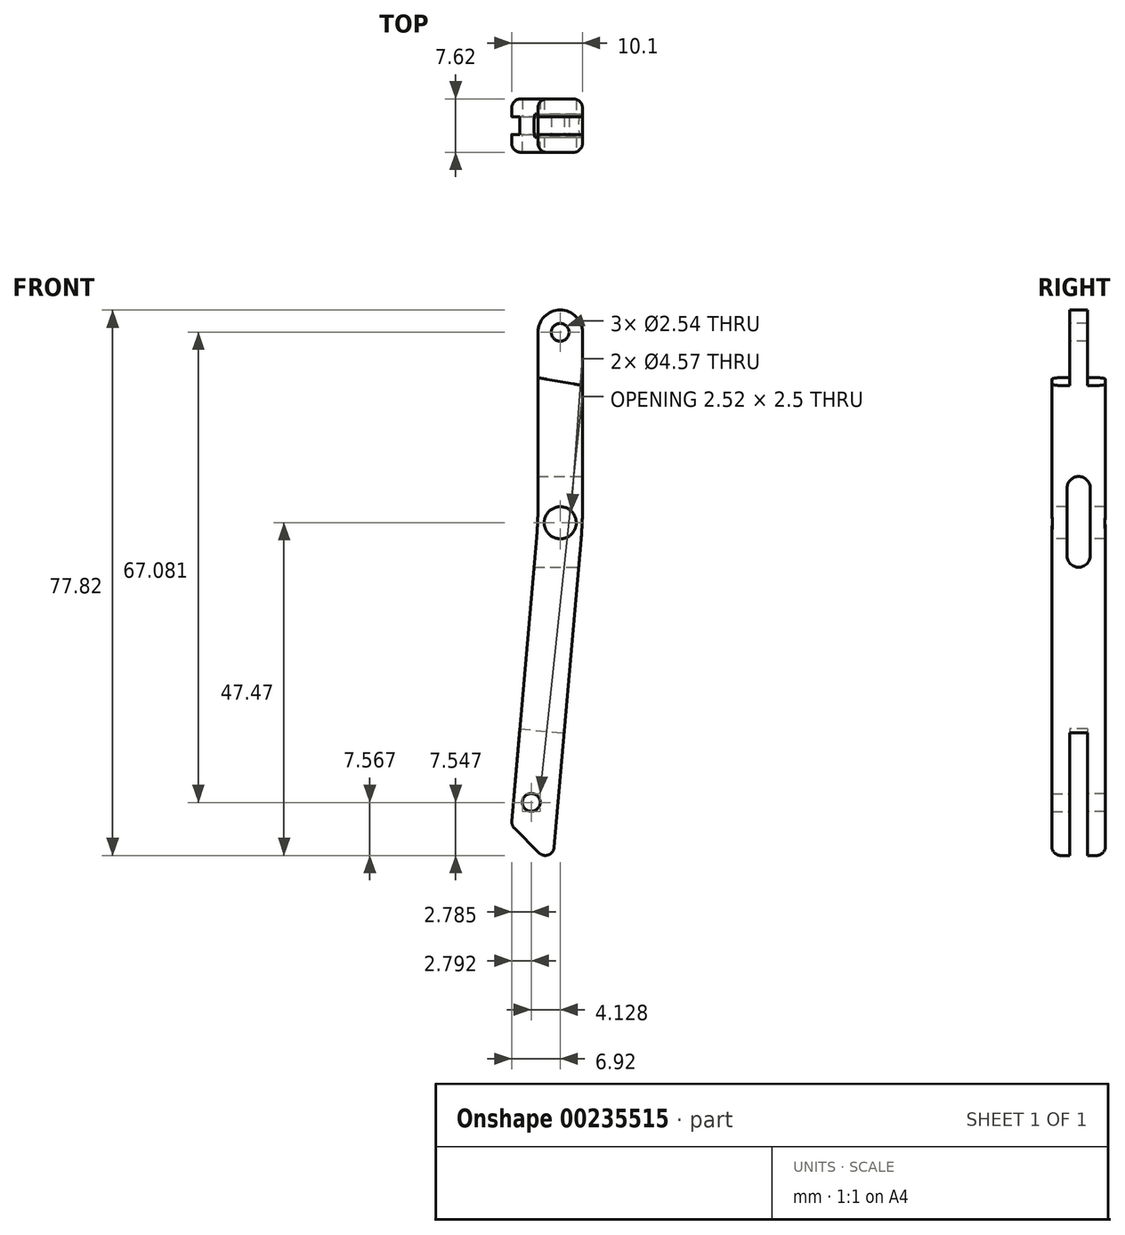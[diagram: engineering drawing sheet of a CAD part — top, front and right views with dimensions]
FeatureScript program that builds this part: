
annotation { "Feature Type Name" : "Feature", "Feature Type Description" : "" }
export const myFeature = defineFeature(function(context is Context, id is Id, definition is map)
    precondition{}
    {
        {
            var Q0;
            Q0=qCreatedBy(makeId("Front.planeOp"),FACE);
            var sketch = newSketch(context, id + "F0", { "sketchPlane" : qUnion([Q0])});
            skLineSegment(sketch, "E0", {"start": v(0, 27.18) * mm, "end": v(0, 0) * mm, "construction": true});
            skLineSegment(sketch, "E1", {"start": v(0, 0) * mm, "end": v(-3.28, -37.48) * mm, "construction": true});
            skPoint(sketch, "E2", {"position": v(0, 0) * mm});
            skLineSegment(sketch, "E3.0", {"start": v(3.17, 27.18) * mm, "end": v(3.18, 2.08) * mm});
            skLineSegment(sketch, "E4.0", {"start": v(2.98, -2.35) * mm, "end": v(-1.1, -49.02) * mm});
            skLineSegment(sketch, "E5.0", {"start": v(-3.18, 27.18) * mm, "end": v(-3.17, 2.36) * mm});
            skLineSegment(sketch, "E6.0", {"start": v(-3.37, -2.07) * mm, "end": v(-6.96, -43.16) * mm});
            skArc(sketch, "E7", {"start": v(2.98, -2.35) * mm, "mid": v(3.13, -0.14) * mm, "end": v(3.17, 2.08) * mm});
            skArc(sketch, "E8", {"start": v(-3.37, -2.07) * mm, "mid": v(-3.22, 0.14) * mm, "end": v(-3.17, 2.36) * mm});
            skLineSegment(sketch, "E9", {"start": v(-3.18, 27.18) * mm, "end": v(3.17, 27.18) * mm, "construction": true});
            skArc(sketch, "E10", {"start": v(3.17, 27.18) * mm, "mid": v(0, 30.35) * mm, "end": v(-3.18, 27.18) * mm});
            skLineSegment(sketch, "E11", {"start": v(-3.18, 20.7) * mm, "end": v(3.18, 19.58) * mm});
            skPoint(sketch, "E12", {"position": v(0, 30.35) * mm});
            skCircle(sketch, "E13", {"center": v(0, 27.18) * mm, "radius": 1.27 * mm});
            skLineSegment(sketch, "E14", {"start": v(-1.1, -49.02) * mm, "end": v(-6.96, -43.16) * mm});
            skPoint(sketch, "E15.orphan", {"position": v(-7.45, -48.74) * mm});
            skCircle(sketch, "E16", {"center": v(0, 0) * mm, "radius": 2.29 * mm});
            skLineSegment(sketch, "E17", {"start": v(-5.76, -29.42) * mm, "end": v(0.56, -29.97) * mm});
            skCircle(sketch, "E18", {"center": v(-4.13, -39.9) * mm, "radius": 1.27 * mm});
            skLineSegment(sketch, "E19", {"start": v(-1.1, -49.02) * mm, "end": v(-19.7, -49.02) * mm, "construction": true});
            skSolve(sketch);
        }
        {
            var Q0;
            {var subQ5=sQuery(id+"F0.wireOp",EDGE,"E7");Q0=makeQuery(id+"F0.imprint","IMPRINT",FACE,{"disambiguationData":[TD([[makeQuery(id+"F0.imprint","IMPRINT",EDGE,{"derivedFrom":subQ5}),1.0]])]});}
            var Q1;
            {var subQ1=sQuery(id+"F0.wireOp",EDGE,"E14");Q1=makeQuery(id+"F0.imprint","IMPRINT",FACE,{"disambiguationData":[TD([[makeQuery(id+"F0.imprint","IMPRINT",EDGE,{"derivedFrom":subQ1}),-1.0]])]});}
            extrude(context, id + "F1", {"entities" : qUnion([Q0, Q1]), "oppositeDirection" : true, "depth" : 3.8 * mm});
        }
        {
            var Q0;
            {var subQ1=sQuery(id+"F0.wireOp",EDGE,"E10");Q0=makeQuery(id+"F0.imprint","IMPRINT",FACE,{"disambiguationData":[TD([[makeQuery(id+"F0.imprint","IMPRINT",EDGE,{"derivedFrom":subQ1}),1.0]])]});}
            extrude(context, id + "F2", {"entities" : qUnion([Q0]), "operationType" : NewBodyOperationType.ADD, "oppositeDirection" : true, "depth" : 1.27 * mm});
        }
        {
            var Q0;
            {var subQ1=sQuery(id+"F0.wireOp",EDGE,"E14");Q0=makeQuery(id+"F0.imprint","IMPRINT",FACE,{"disambiguationData":[TD([[makeQuery(id+"F0.imprint","IMPRINT",EDGE,{"derivedFrom":subQ1}),-1.0]])]});}
            extrude(context, id + "F3", {"entities" : qUnion([Q0]), "operationType" : NewBodyOperationType.REMOVE, "oppositeDirection" : true, "depth" : 1.27 * mm});
        }
        {
            var Q0;
            Q0=makeQuery(id+"F1.opExtrude","SWEPT_BODY",BODY,{"disambiguationData":[OSD([sQuery(id+"F0.wireOp",EDGE,"E3.0"),sQuery(id+"F0.wireOp",EDGE,"E4.0"),sQuery(id+"F0.wireOp",EDGE,"E5.0"),sQuery(id+"F0.wireOp",EDGE,"E6.0"),sQuery(id+"F0.wireOp",EDGE,"E7"),sQuery(id+"F0.wireOp",EDGE,"E8"),sQuery(id+"F0.wireOp",EDGE,"E11"),sQuery(id+"F0.wireOp",EDGE,"E14"),sQuery(id+"F0.wireOp",EDGE,"E16"),sQuery(id+"F0.wireOp",EDGE,"E18")])]});
            var Q1;
            Q1=qCreatedBy(makeId("Front.planeOp"),FACE);
            mirror(context, id + "F4", {"operationType" : NewBodyOperationType.ADD, "entities" : qUnion([Q0]), "mirrorPlane" : qUnion([Q1])});
        }
        {
            var Q0;
            Q0=qCreatedBy(makeId("Right.planeOp"),FACE);
            var sketch = newSketch(context, id + "F5", { "sketchPlane" : qUnion([Q0])});
            skArc(sketch, "E20", {"start": v(1.65, 4.95) * mm, "mid": v(0, 6.6) * mm, "end": v(-1.65, 4.95) * mm});
            skArc(sketch, "E21", {"start": v(-1.65, -4.7) * mm, "mid": v(0, -6.35) * mm, "end": v(1.65, -4.7) * mm});
            skLineSegment(sketch, "E22", {"start": v(-1.65, 4.95) * mm, "end": v(-1.65, -4.7) * mm});
            skLineSegment(sketch, "E23", {"start": v(1.65, 4.95) * mm, "end": v(1.65, -4.7) * mm});
            skSolve(sketch);
        }
        {
            var Q0;
            Q0 = qSketchRegion(id + "F5", true);
            extrude(context, id + "F6", {"entities" : qUnion([Q0]), "operationType" : NewBodyOperationType.REMOVE, "endBound" : BoundingType.SYMMETRIC, "oppositeDirection" : true, "depth" : 25.4 * mm});
        }
        {
            var Q0;
            Q0=makeQuery(id+"F1.opExtrude","SWEPT_EDGE",EDGE,{"disambiguationData":[OSD([sQuery(id+"F0.wireOp",EDGE,"E4.0"),sQuery(id+"F0.wireOp",EDGE,"E14")])]});
            var Q1;
            Q1=makeQuery(id+"F4.opPattern","COPY",EDGE,{"derivedFrom":makeQuery(id+"F1.opExtrude","SWEPT_EDGE",EDGE,{"disambiguationData":[OSD([sQuery(id+"F0.wireOp",EDGE,"E4.0"),sQuery(id+"F0.wireOp",EDGE,"E14")])]}),"instanceName":"1"});
            var Q2;
            Q2=makeQuery(id+"F4.opPattern","COPY",EDGE,{"derivedFrom":makeQuery(id+"F1.opExtrude","SWEPT_EDGE",EDGE,{"disambiguationData":[OSD([sQuery(id+"F0.wireOp",EDGE,"E6.0"),sQuery(id+"F0.wireOp",EDGE,"E14")])]}),"instanceName":"1"});
            var Q3;
            Q3=makeQuery(id+"F1.opExtrude","SWEPT_EDGE",EDGE,{"disambiguationData":[OSD([sQuery(id+"F0.wireOp",EDGE,"E6.0"),sQuery(id+"F0.wireOp",EDGE,"E14")])]});
            fillet(context, id + "F7", {"entities" : qUnion([Q0, Q1, Q2, Q3]), "radius" : 1.27 * mm, "tangentPropagation" : true, "allowEdgeOverflow" : false});
        }
        {
            var Q0;
            Q0=makeQuery(id+"F1.opExtrude","CAP_EDGE",EDGE,{"disambiguationData":[OSD([sQuery(id+"F0.wireOp",EDGE,"E4.0")])],"isStart":false});
            var Q1;
            Q1=makeQuery(id+"F1.opExtrude","CAP_EDGE",EDGE,{"disambiguationData":[OSD([sQuery(id+"F0.wireOp",EDGE,"E3.0")])],"isStart":false});
            var Q2;
            Q2=makeQuery(id+"F1.opExtrude","CAP_EDGE",EDGE,{"disambiguationData":[OSD([sQuery(id+"F0.wireOp",EDGE,"E7")])],"isStart":false});
            var Q3;
            Q3=makeQuery(id+"F4.opPattern","COPY",EDGE,{"derivedFrom":makeQuery(id+"F1.opExtrude","CAP_EDGE",EDGE,{"disambiguationData":[OSD([sQuery(id+"F0.wireOp",EDGE,"E4.0")])],"isStart":false}),"instanceName":"1"});
            var Q4;
            Q4=makeQuery(id+"F4.opPattern","COPY",EDGE,{"derivedFrom":makeQuery(id+"F1.opExtrude","CAP_EDGE",EDGE,{"disambiguationData":[OSD([sQuery(id+"F0.wireOp",EDGE,"E7")])],"isStart":false}),"instanceName":"1"});
            var Q5;
            Q5=makeQuery(id+"F4.opPattern","COPY",EDGE,{"derivedFrom":makeQuery(id+"F1.opExtrude","CAP_EDGE",EDGE,{"disambiguationData":[OSD([sQuery(id+"F0.wireOp",EDGE,"E3.0")])],"isStart":false}),"instanceName":"1"});
            var Q6;
            Q6=makeQuery(id+"F4.opPattern","COPY",EDGE,{"derivedFrom":makeQuery(id+"F1.opExtrude","CAP_EDGE",EDGE,{"disambiguationData":[OSD([sQuery(id+"F0.wireOp",EDGE,"E8")])],"isStart":false}),"instanceName":"1"});
            var Q7;
            Q7=makeQuery(id+"F4.opPattern","COPY",EDGE,{"derivedFrom":makeQuery(id+"F1.opExtrude","CAP_EDGE",EDGE,{"disambiguationData":[OSD([sQuery(id+"F0.wireOp",EDGE,"E6.0")])],"isStart":false}),"instanceName":"1"});
            var Q8;
            Q8=makeQuery(id+"F1.opExtrude","CAP_EDGE",EDGE,{"disambiguationData":[OSD([sQuery(id+"F0.wireOp",EDGE,"E6.0")])],"isStart":false});
            fillet(context, id + "F8", {"entities" : qUnion([Q0, Q1, Q2, Q3, Q4, Q5, Q6, Q7, Q8]), "radius" : 1.27 * mm, "tangentPropagation" : true, "allowEdgeOverflow" : false});
        }
    });
